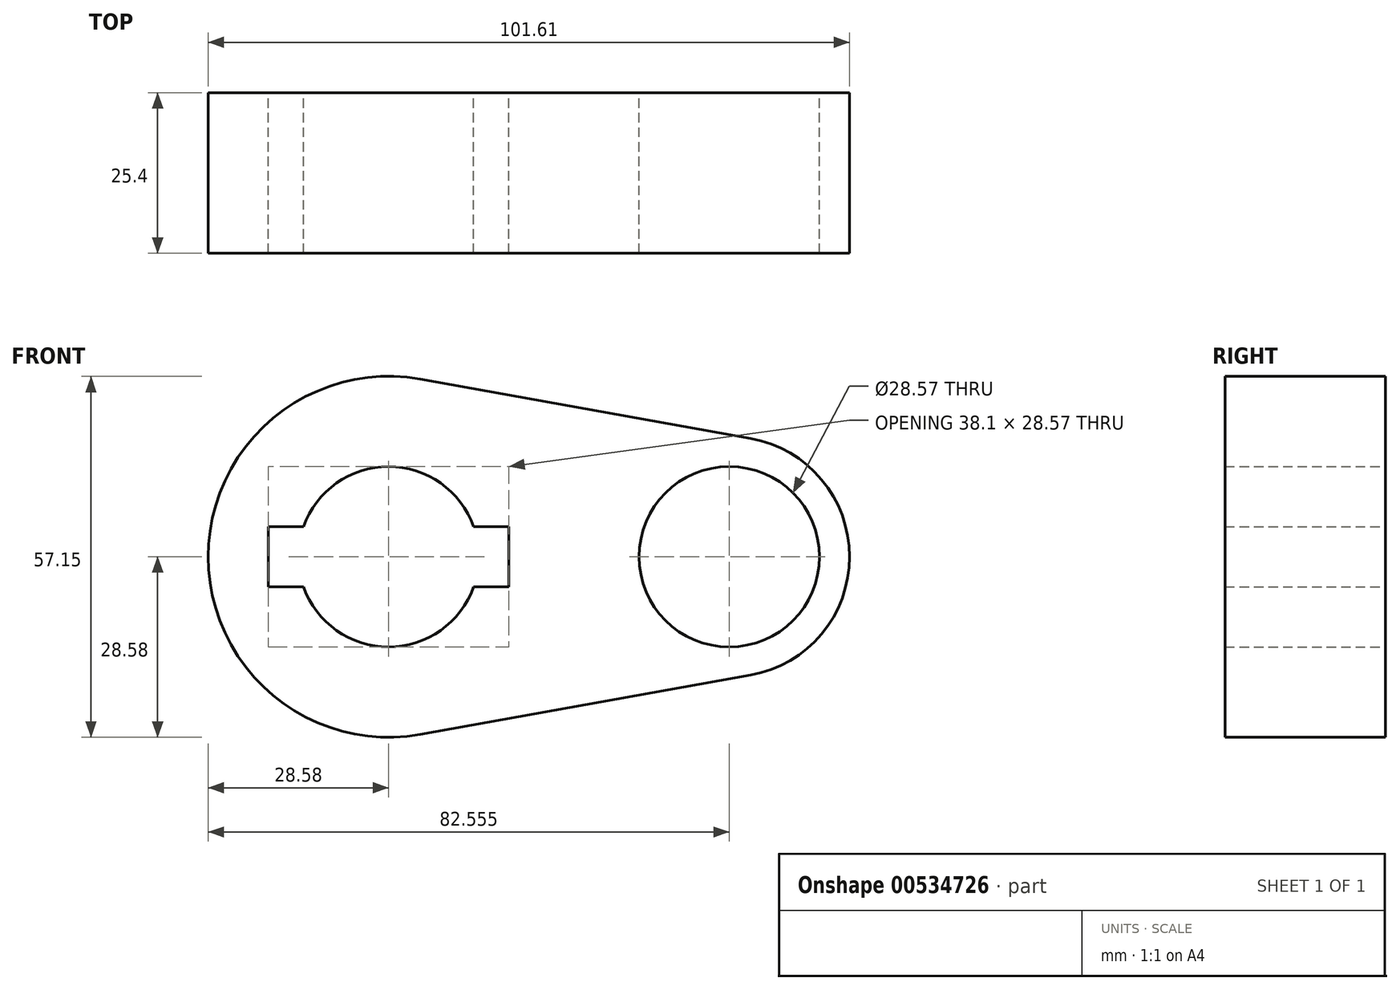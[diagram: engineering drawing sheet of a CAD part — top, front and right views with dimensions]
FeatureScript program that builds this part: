
annotation { "Feature Type Name" : "Feature", "Feature Type Description" : "" }
export const myFeature = defineFeature(function(context is Context, id is Id, definition is map)
    precondition{}
    {
        {
            var Q0;
            Q0=qCreatedBy(makeId("Front.planeOp"),FACE);
            var sketch = newSketch(context, id + "F0", { "sketchPlane" : qUnion([Q0])});
            skCircle(sketch, "E0", {"center": v(0, 0) * mm, "radius": 28.58 * mm});
            skCircle(sketch, "E1", {"center": v(53.98, 0) * mm, "radius": 19.05 * mm});
            skLineSegment(sketch, "E2", {"start": v(5.04, 28.13) * mm, "end": v(57.34, 18.75) * mm});
            skLineSegment(sketch, "E3", {"start": v(5.04, -28.13) * mm, "end": v(57.34, -18.75) * mm});
            skCircle(sketch, "E4", {"center": v(53.98, 0) * mm, "radius": 14.29 * mm});
            skCircle(sketch, "E5", {"center": v(0, 0) * mm, "radius": 14.29 * mm});
            skLineSegment(sketch, "E6.bottom", {"start": v(19.05, -4.76) * mm, "end": v(-19.05, -4.76) * mm});
            skLineSegment(sketch, "E6.top", {"start": v(19.05, 4.76) * mm, "end": v(-19.05, 4.76) * mm});
            skLineSegment(sketch, "E6.left", {"start": v(19.05, -4.76) * mm, "end": v(19.05, 4.76) * mm});
            skLineSegment(sketch, "E6.right", {"start": v(-19.05, -4.76) * mm, "end": v(-19.05, 4.76) * mm});
            skSolve(sketch);
        }
        {
            var Q0;
            Q0 = qSketchRegion(id + "F0", true);
            extrude(context, id + "F1", {"entities" : qUnion([Q0]), "depth" : 25.4 * mm, "offsetDistance" : 25.4 * mm});
        }
    });
